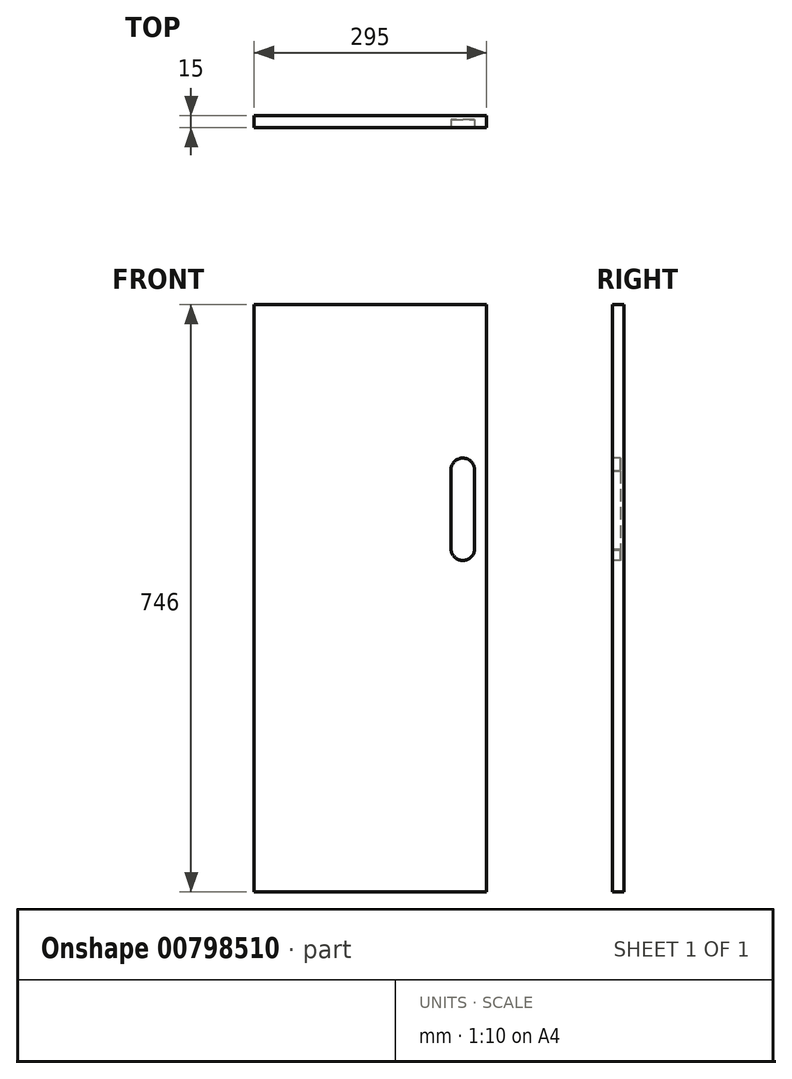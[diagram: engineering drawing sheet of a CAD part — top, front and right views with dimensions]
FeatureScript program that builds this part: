
annotation { "Feature Type Name" : "Feature", "Feature Type Description" : "" }
export const myFeature = defineFeature(function(context is Context, id is Id, definition is map)
    precondition{}
    {
        {
            var Q0;
            Q0=qCreatedBy(makeId("Front.planeOp"),FACE);
            var sketch = newSketch(context, id + "F0", { "sketchPlane" : qUnion([Q0])});
            skLineSegment(sketch, "E0.bottom", {"start": v(-147.5, 373) * mm, "end": v(147.5, 373) * mm});
            skLineSegment(sketch, "E0.top", {"start": v(-147.5, -373) * mm, "end": v(147.5, -373) * mm});
            skLineSegment(sketch, "E0.left", {"start": v(-147.5, 373) * mm, "end": v(-147.5, -373) * mm});
            skLineSegment(sketch, "E0.right", {"start": v(147.5, 373) * mm, "end": v(147.5, -373) * mm});
            skSolve(sketch);
        }
        {
            var Q0;
            Q0=makeQuery(id+"F0.imprint","IMPRINT",FACE,{"disambiguationData":[TD([[makeQuery(id+"F0.imprint","IMPRINT",EDGE,{"derivedFrom":sQuery(id+"F0.wireOp",EDGE,"E0.bottom")}),-1.0]])]});
            extrude(context, id + "F1", {"entities" : qUnion([Q0]), "depth" : 15 * mm, "offsetDistance" : 25 * mm});
        }
        {
            var Q0;
            Q0=makeQuery(id+"F1.opExtrude","CAP_FACE",FACE,{"disambiguationData":[OSD([sQuery(id+"F0.wireOp",EDGE,"E0.bottom"),sQuery(id+"F0.wireOp",EDGE,"E0.top"),sQuery(id+"F0.wireOp",EDGE,"E0.left"),sQuery(id+"F0.wireOp",EDGE,"E0.right")])],"isStart":false});
            var sketch = newSketch(context, id + "F2", { "sketchPlane" : qUnion([Q0])});
            skCircle(sketch, "E1", {"center": v(117.5, 163) * mm, "radius": 15 * mm});
            skCircle(sketch, "E2", {"center": v(117.5, 63) * mm, "radius": 15 * mm});
            skLineSegment(sketch, "E3", {"start": v(102.68, 160.7) * mm, "end": v(102.68, 60.7) * mm});
            skLineSegment(sketch, "E4", {"start": v(132.44, 161.66) * mm, "end": v(132.44, 61.66) * mm});
            skSolve(sketch);
        }
        {
            var Q0;
            {var subQ0=sQuery(id+"F2.wireOp",EDGE,"E1");var subQ1=makeQuery(id+"F2.imprint","INTERSECT",VERTEX,{"derivedFrom":[subQ0,sQuery(id+"F2.wireOp",EDGE,"E3")]});Q0=makeQuery(id+"F2.imprint","IMPRINT",FACE,{"disambiguationData":[TD([[makeQuery(id+"F2.imprint","IMPRINT",EDGE,{"disambiguationData":[TD([[subQ1,-1.0]])],"derivedFrom":subQ0}),1.0]])]});}
            var Q1;
            {var subQ0=sQuery(id+"F2.wireOp",EDGE,"E3");var subQ1=sQuery(id+"F2.wireOp",EDGE,"E1");var subQ2=makeQuery(id+"F2.imprint","INTERSECT",VERTEX,{"derivedFrom":[subQ1,subQ0]});Q1=makeQuery(id+"F2.imprint","IMPRINT",FACE,{"disambiguationData":[TD([[makeQuery(id+"F2.imprint","IMPRINT",EDGE,{"disambiguationData":[TD([[subQ2,-1.0]])],"derivedFrom":subQ1}),-1.0]])]});}
            var Q2;
            {var subQ0=sQuery(id+"F2.wireOp",EDGE,"E3");var subQ1=sQuery(id+"F2.wireOp",EDGE,"E2");var subQ2=makeQuery(id+"F2.imprint","INTERSECT",VERTEX,{"disambiguationData":[OD(1.0)],"derivedFrom":[subQ1,subQ0]});Q2=makeQuery(id+"F2.imprint","IMPRINT",FACE,{"disambiguationData":[TD([[makeQuery(id+"F2.imprint","IMPRINT",EDGE,{"disambiguationData":[TD([[subQ2,1.0]])],"derivedFrom":subQ1}),1.0]])]});}
            extrude(context, id + "F3", {"entities" : qUnion([Q0, Q1, Q2]), "operationType" : NewBodyOperationType.REMOVE, "oppositeDirection" : true, "depth" : 10 * mm, "offsetDistance" : 25 * mm});
        }
    });
